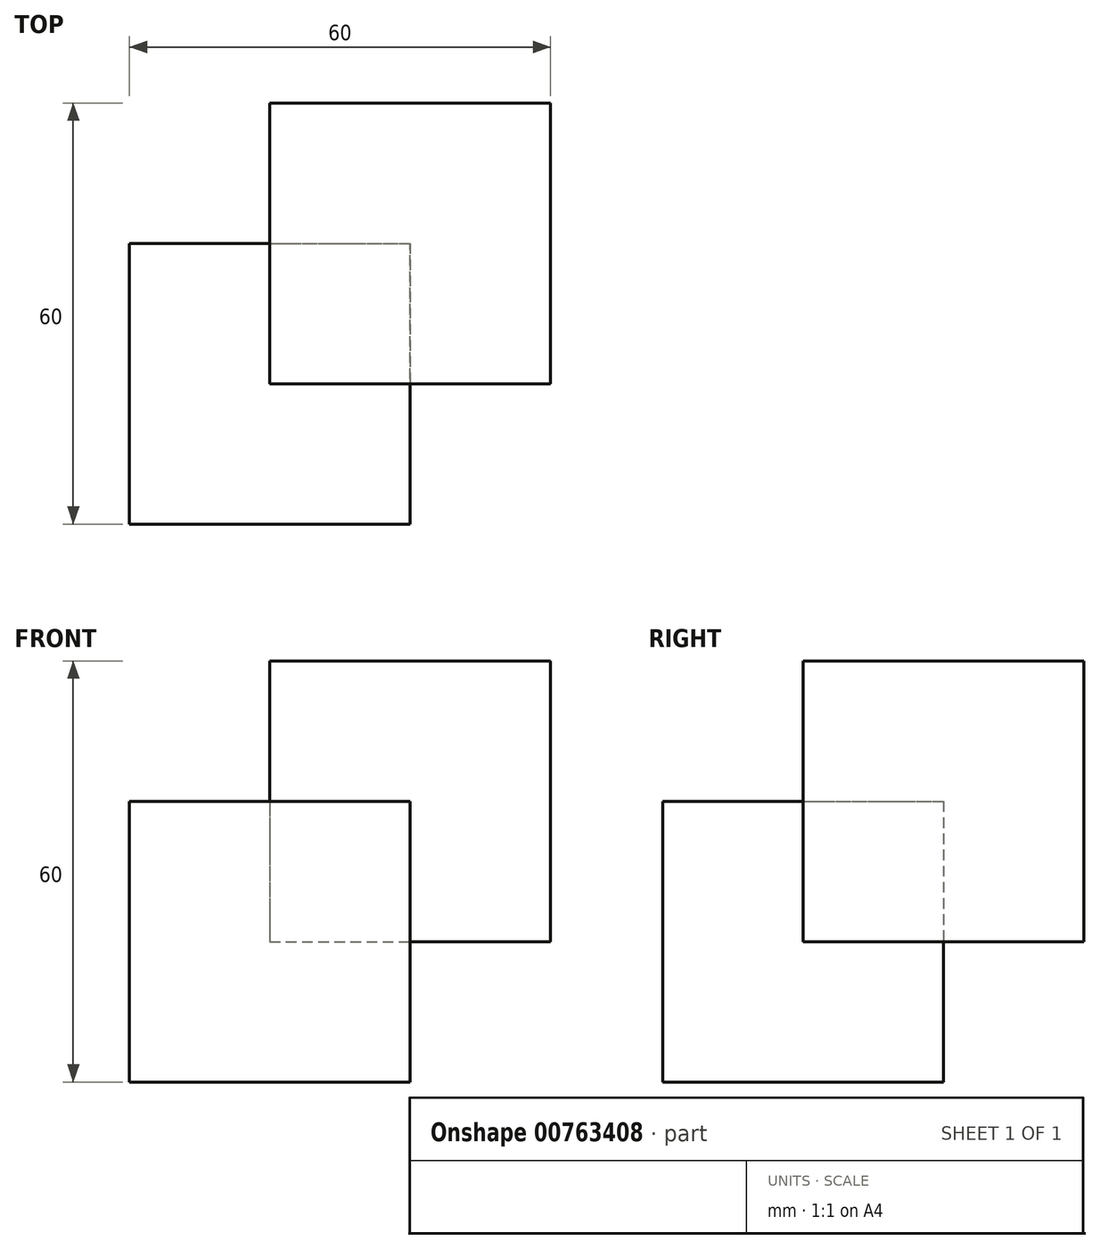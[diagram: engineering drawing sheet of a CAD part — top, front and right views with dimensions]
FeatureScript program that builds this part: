
annotation { "Feature Type Name" : "Feature", "Feature Type Description" : "" }
export const myFeature = defineFeature(function(context is Context, id is Id, definition is map)
    precondition{}
    {
        {
            var Q0;
            Q0=qCreatedBy(makeId("Top.planeOp"),FACE);
            var sketch = newSketch(context, id + "F0", { "sketchPlane" : qUnion([Q0])});
            skLineSegment(sketch, "E0.bottom", {"start": v(-20, -20) * mm, "end": v(20, -20) * mm});
            skLineSegment(sketch, "E0.top", {"start": v(-20, 20) * mm, "end": v(20, 20) * mm});
            skLineSegment(sketch, "E0.left", {"start": v(-20, -20) * mm, "end": v(-20, 20) * mm});
            skLineSegment(sketch, "E0.right", {"start": v(20, -20) * mm, "end": v(20, 20) * mm});
            skPoint(sketch, "E0.middle", {"position": v(0, 0) * mm});
            skSolve(sketch);
        }
        {
            var Q0;
            Q0 = qSketchRegion(id + "F0", true);
            extrude(context, id + "F1", {"entities" : qUnion([Q0]), "endBound" : BoundingType.SYMMETRIC, "depth" : 40 * mm, "offsetDistance" : 25 * mm});
        }
        {
            var Q0;
            Q0=makeQuery(id+"F1.opExtrude","SWEPT_BODY",BODY,{"disambiguationData":[OSD([sQuery(id+"F0.wireOp",EDGE,"E0.bottom"),sQuery(id+"F0.wireOp",EDGE,"E0.top"),sQuery(id+"F0.wireOp",EDGE,"E0.left"),sQuery(id+"F0.wireOp",EDGE,"E0.right")])]});
            transform(context, id + "F2", {"entities" : qUnion([Q0]), "transformType" : TransformType.TRANSLATION_3D, "dx" : 20 * mm, "dy" : 20 * mm, "dz" : 20 * mm, "makeCopy" : true});
        }
        {
            var Q0;
            Q0=makeQuery(id+"F2.opPattern","COPY",BODY,{"derivedFrom":makeQuery(id+"F1.opExtrude","SWEPT_BODY",BODY,{"disambiguationData":[OSD([sQuery(id+"F0.wireOp",EDGE,"E0.bottom"),sQuery(id+"F0.wireOp",EDGE,"E0.top"),sQuery(id+"F0.wireOp",EDGE,"E0.left"),sQuery(id+"F0.wireOp",EDGE,"E0.right")])]}),"instanceName":"1"});
            var Q1;
            Q1=makeQuery(id+"F1.opExtrude","SWEPT_BODY",BODY,{"disambiguationData":[OSD([sQuery(id+"F0.wireOp",EDGE,"E0.bottom"),sQuery(id+"F0.wireOp",EDGE,"E0.top"),sQuery(id+"F0.wireOp",EDGE,"E0.left"),sQuery(id+"F0.wireOp",EDGE,"E0.right")])]});
            var Q2;
            Q2=makeQuery(id+"F1.opExtrude","SWEPT_BODY",BODY,{"disambiguationData":[OSD([sQuery(id+"F0.wireOp",EDGE,"E0.bottom"),sQuery(id+"F0.wireOp",EDGE,"E0.top"),sQuery(id+"F0.wireOp",EDGE,"E0.left"),sQuery(id+"F0.wireOp",EDGE,"E0.right")])]});
            booleanBodies(context, id + "F3", {"operationType" : BooleanOperationType.INTERSECTION, "tools" : qUnion([Q0, Q1]), "targets" : qUnion([Q2]), "keepTools" : true});
        }
    });
